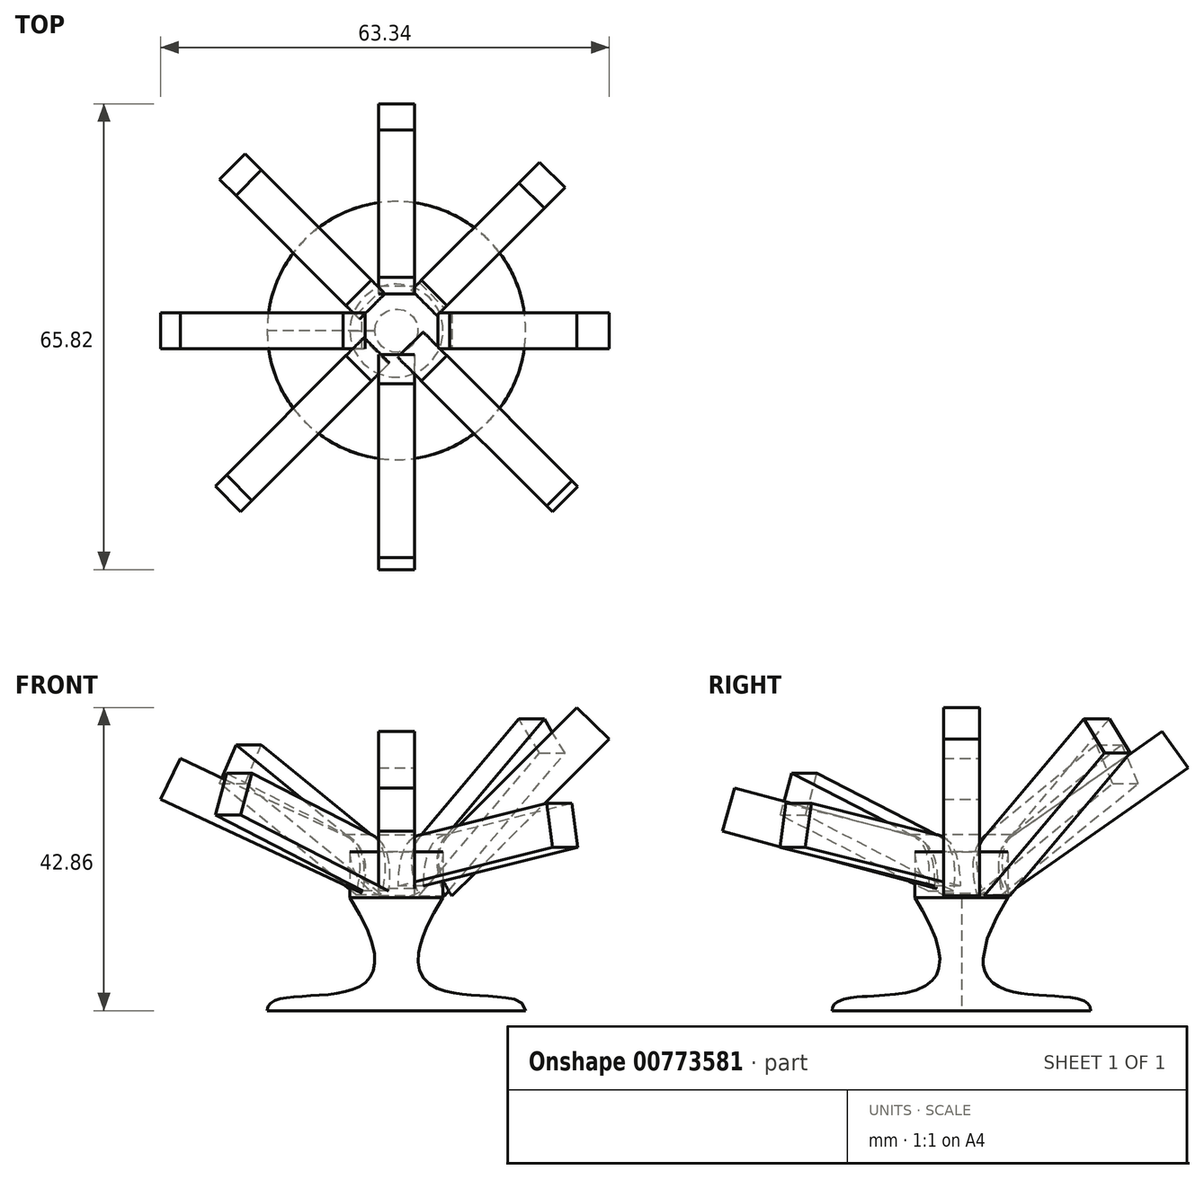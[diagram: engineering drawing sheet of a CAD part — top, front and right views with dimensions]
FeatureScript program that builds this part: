
annotation { "Feature Type Name" : "Feature", "Feature Type Description" : "" }
export const myFeature = defineFeature(function(context is Context, id is Id, definition is map)
    precondition{}
    {
        {
            assignVariable(context, id + "F0", {"name" : "First", "anyValue" : 45});
        }
        {
            assignVariable(context, id + "F1", {"name" : "delta", "anyValue" : -5});
        }
        {
            assignVariable(context, id + "F2", {"name" : "Count", "anyValue" : 8});
        }
        {
            var Q0;
            Q0=qCreatedBy(makeId("Front.planeOp"),FACE);
            var sketch = newSketch(context, id + "F3", { "sketchPlane" : qUnion([Q0])});
            skLineSegment(sketch, "E0", {"start": v(6.57, 22.45) * mm, "end": v(6.57, 15.95) * mm});
            skLineSegment(sketch, "E1", {"start": v(0, 0) * mm, "end": v(18.25, 0) * mm});
            skLineSegment(sketch, "E2", {"start": v(0, 0) * mm, "end": v(0, 28.99) * mm});
            skFitSpline(sketch, "E3", {"points": [v(6.57, 15.95) * mm, v(18.25, 0) * mm], "startDerivative": vector(-37.1, -59.05) * mm, "endDerivative": vector(-0.41, -15.66) * mm});
            skArc(sketch, "E4", {"start": v(6.57, 22.45) * mm, "mid": v(4.64, 27.09) * mm, "end": v(0, 28.99) * mm});
            skSolve(sketch);
        }
        {
            var Q0;
            Q0=makeQuery(id+"F3.imprint","IMPRINT",FACE,{"disambiguationData":[TD([[makeQuery(id+"F3.imprint","IMPRINT",EDGE,{"derivedFrom":sQuery(id+"F3.wireOp",EDGE,"E0")}),-1.0]])]});
            var Q1;
            Q1=sQuery(id+"F3.wireOp",EDGE,"E2");
            revolve(context, id + "F4", {"surfaceOperationType" : NewSurfaceOperationType.NEW, "entities" : qUnion([Q0]), "axis" : qUnion([Q1]), "revolveType" : RevolveType.FULL});
        }
        {
            var Q0;
            Q0=qCreatedBy(makeId("Front.planeOp"),FACE);
            var sketch = newSketch(context, id + "F5", { "sketchPlane" : qUnion([Q0])});
            skLineSegment(sketch, "E5", {"start": v(32.93, 24.9) * mm, "end": v(7.53, 24.9) * mm});
            skLineSegment(sketch, "E6", {"start": v(1.61, 18.55) * mm, "end": v(33, 18.55) * mm});
            skLineSegment(sketch, "E7", {"start": v(33, 18.55) * mm, "end": v(32.93, 24.9) * mm});
            skFitSpline(sketch, "E8", {"points": [v(7.53, 24.9) * mm, v(1.61, 18.55) * mm], "startDerivative": vector(-9.34, 0.31) * mm, "endDerivative": vector(-2.73, -13.53) * mm});
            skSolve(sketch);
        }
        {
            var Q0;
            Q0=makeQuery(id+"F5.imprint","IMPRINT",FACE,{"disambiguationData":[TD([[makeQuery(id+"F5.imprint","IMPRINT",EDGE,{"derivedFrom":sQuery(id+"F5.wireOp",EDGE,"E5")}),1.0]])]});
            extrude(context, id + "F6", {"entities" : qUnion([Q0]), "endBound" : BoundingType.SYMMETRIC, "oppositeDirection" : true, "depth" : 5.08 * mm, "offsetDistance" : 25.4 * mm});
        }
        {
            var Q0;
            Q0=makeQuery(id+"F6.opExtrude","SWEPT_BODY",BODY,{"disambiguationData":[OSD([sQuery(id+"F5.wireOp",EDGE,"E5"),sQuery(id+"F5.wireOp",EDGE,"E6"),sQuery(id+"F5.wireOp",EDGE,"E7"),sQuery(id+"F5.wireOp",EDGE,"E8")])]});
            var Q1;
            Q1=sQuery(id+"F3.wireOp",EDGE,"E2");
            circularPattern(context, id + "F7", {"entities" : qUnion([Q0]), "axis" : qUnion([Q1]), "angle" : 360 * degree, "instanceCount" : getVariable(context, 'Count'), "equalSpace" : true});
        }
        {
            var Q0;
            Q0=makeQuery(id+"F6.opExtrude","SWEPT_BODY",BODY,{"disambiguationData":[OSD([sQuery(id+"F5.wireOp",EDGE,"E5"),sQuery(id+"F5.wireOp",EDGE,"E6"),sQuery(id+"F5.wireOp",EDGE,"E7"),sQuery(id+"F5.wireOp",EDGE,"E8")])]});
            var Q1;
            Q1=makeQuery(id+"F6.opExtrude","SWEPT_EDGE",EDGE,{"disambiguationData":[OSD([sQuery(id+"F5.wireOp",EDGE,"E5"),sQuery(id+"F5.wireOp",EDGE,"E8")])]});
            transform(context, id + "F8", {"entities" : qUnion([Q0]), "transformType" : TransformType.ROTATION, "transformAxis" : qUnion([Q1]), "angle" : (getVariable(context, 'First')) * degree, "makeCopy" : false});
        }
        {
            var Q0;
            Q0=makeQuery(id+"F7.opPattern","COPY",BODY,{"derivedFrom":makeQuery(id+"F6.opExtrude","SWEPT_BODY",BODY,{"disambiguationData":[OSD([sQuery(id+"F5.wireOp",EDGE,"E5"),sQuery(id+"F5.wireOp",EDGE,"E6"),sQuery(id+"F5.wireOp",EDGE,"E7"),sQuery(id+"F5.wireOp",EDGE,"E8")])]}),"instanceName":"1"});
            var Q1;
            Q1=makeQuery(id+"F7.opPattern","COPY",EDGE,{"derivedFrom":makeQuery(id+"F6.opExtrude","SWEPT_EDGE",EDGE,{"disambiguationData":[OSD([sQuery(id+"F5.wireOp",EDGE,"E5"),sQuery(id+"F5.wireOp",EDGE,"E8")])]}),"instanceName":"1"});
            transform(context, id + "F9", {"entities" : qUnion([Q0]), "transformType" : TransformType.ROTATION, "transformAxis" : qUnion([Q1]), "angle" : (getVariable(context, 'First') + getVariable(context, 'delta')) * degree, "makeCopy" : false});
        }
        {
            var Q0;
            Q0=makeQuery(id+"F7.opPattern","COPY",BODY,{"derivedFrom":makeQuery(id+"F6.opExtrude","SWEPT_BODY",BODY,{"disambiguationData":[OSD([sQuery(id+"F5.wireOp",EDGE,"E5"),sQuery(id+"F5.wireOp",EDGE,"E6"),sQuery(id+"F5.wireOp",EDGE,"E7"),sQuery(id+"F5.wireOp",EDGE,"E8")])]}),"instanceName":"2"});
            var Q1;
            Q1=makeQuery(id+"F7.opPattern","COPY",EDGE,{"derivedFrom":makeQuery(id+"F6.opExtrude","SWEPT_EDGE",EDGE,{"disambiguationData":[OSD([sQuery(id+"F5.wireOp",EDGE,"E5"),sQuery(id+"F5.wireOp",EDGE,"E8")])]}),"instanceName":"2"});
            transform(context, id + "F10", {"entities" : qUnion([Q0]), "transformType" : TransformType.ROTATION, "transformAxis" : qUnion([Q1]), "angle" : (getVariable(context, 'First') + 2 * getVariable(context, 'delta')) * degree, "makeCopy" : false});
        }
        {
            var Q0;
            Q0=makeQuery(id+"F7.opPattern","COPY",BODY,{"derivedFrom":makeQuery(id+"F6.opExtrude","SWEPT_BODY",BODY,{"disambiguationData":[OSD([sQuery(id+"F5.wireOp",EDGE,"E5"),sQuery(id+"F5.wireOp",EDGE,"E6"),sQuery(id+"F5.wireOp",EDGE,"E7"),sQuery(id+"F5.wireOp",EDGE,"E8")])]}),"instanceName":"3"});
            var Q1;
            Q1=makeQuery(id+"F7.opPattern","COPY",EDGE,{"derivedFrom":makeQuery(id+"F6.opExtrude","SWEPT_EDGE",EDGE,{"disambiguationData":[OSD([sQuery(id+"F5.wireOp",EDGE,"E5"),sQuery(id+"F5.wireOp",EDGE,"E8")])]}),"instanceName":"3"});
            transform(context, id + "F11", {"entities" : qUnion([Q0]), "transformType" : TransformType.ROTATION, "transformAxis" : qUnion([Q1]), "angle" : (getVariable(context, 'First') + 3 * getVariable(context, 'delta')) * degree, "makeCopy" : false});
        }
        {
            var Q0;
            Q0=makeQuery(id+"F7.opPattern","COPY",BODY,{"derivedFrom":makeQuery(id+"F6.opExtrude","SWEPT_BODY",BODY,{"disambiguationData":[OSD([sQuery(id+"F5.wireOp",EDGE,"E5"),sQuery(id+"F5.wireOp",EDGE,"E6"),sQuery(id+"F5.wireOp",EDGE,"E7"),sQuery(id+"F5.wireOp",EDGE,"E8")])]}),"instanceName":"4"});
            var Q1;
            Q1=makeQuery(id+"F7.opPattern","COPY",EDGE,{"derivedFrom":makeQuery(id+"F6.opExtrude","SWEPT_EDGE",EDGE,{"disambiguationData":[OSD([sQuery(id+"F5.wireOp",EDGE,"E5"),sQuery(id+"F5.wireOp",EDGE,"E8")])]}),"instanceName":"4"});
            transform(context, id + "F12", {"entities" : qUnion([Q0]), "transformType" : TransformType.ROTATION, "transformAxis" : qUnion([Q1]), "angle" : (getVariable(context, 'First') + 4 * getVariable(context, 'delta')) * degree, "makeCopy" : false});
        }
        {
            var Q0;
            Q0=makeQuery(id+"F7.opPattern","COPY",BODY,{"derivedFrom":makeQuery(id+"F6.opExtrude","SWEPT_BODY",BODY,{"disambiguationData":[OSD([sQuery(id+"F5.wireOp",EDGE,"E5"),sQuery(id+"F5.wireOp",EDGE,"E6"),sQuery(id+"F5.wireOp",EDGE,"E7"),sQuery(id+"F5.wireOp",EDGE,"E8")])]}),"instanceName":"5"});
            var Q1;
            Q1=makeQuery(id+"F7.opPattern","COPY",EDGE,{"derivedFrom":makeQuery(id+"F6.opExtrude","SWEPT_EDGE",EDGE,{"disambiguationData":[OSD([sQuery(id+"F5.wireOp",EDGE,"E5"),sQuery(id+"F5.wireOp",EDGE,"E8")])]}),"instanceName":"5"});
            transform(context, id + "F13", {"entities" : qUnion([Q0]), "transformType" : TransformType.ROTATION, "transformAxis" : qUnion([Q1]), "angle" : (getVariable(context, 'First') + 5 * getVariable(context, 'delta')) * degree, "makeCopy" : false});
        }
        {
            var Q0;
            Q0=makeQuery(id+"F7.opPattern","COPY",BODY,{"derivedFrom":makeQuery(id+"F6.opExtrude","SWEPT_BODY",BODY,{"disambiguationData":[OSD([sQuery(id+"F5.wireOp",EDGE,"E5"),sQuery(id+"F5.wireOp",EDGE,"E6"),sQuery(id+"F5.wireOp",EDGE,"E7"),sQuery(id+"F5.wireOp",EDGE,"E8")])]}),"instanceName":"6"});
            var Q1;
            Q1=makeQuery(id+"F7.opPattern","COPY",EDGE,{"derivedFrom":makeQuery(id+"F6.opExtrude","SWEPT_EDGE",EDGE,{"disambiguationData":[OSD([sQuery(id+"F5.wireOp",EDGE,"E5"),sQuery(id+"F5.wireOp",EDGE,"E8")])]}),"instanceName":"6"});
            transform(context, id + "F14", {"entities" : qUnion([Q0]), "transformType" : TransformType.ROTATION, "transformAxis" : qUnion([Q1]), "angle" : (getVariable(context, 'First') + 6 * getVariable(context, 'delta')) * degree, "makeCopy" : false});
        }
        {
            var Q0;
            Q0=makeQuery(id+"F7.opPattern","COPY",BODY,{"derivedFrom":makeQuery(id+"F6.opExtrude","SWEPT_BODY",BODY,{"disambiguationData":[OSD([sQuery(id+"F5.wireOp",EDGE,"E5"),sQuery(id+"F5.wireOp",EDGE,"E6"),sQuery(id+"F5.wireOp",EDGE,"E7"),sQuery(id+"F5.wireOp",EDGE,"E8")])]}),"instanceName":"7"});
            var Q1;
            Q1=makeQuery(id+"F7.opPattern","COPY",EDGE,{"derivedFrom":makeQuery(id+"F6.opExtrude","SWEPT_EDGE",EDGE,{"disambiguationData":[OSD([sQuery(id+"F5.wireOp",EDGE,"E5"),sQuery(id+"F5.wireOp",EDGE,"E8")])]}),"instanceName":"7"});
            transform(context, id + "F15", {"entities" : qUnion([Q0]), "transformType" : TransformType.ROTATION, "transformAxis" : qUnion([Q1]), "angle" : (getVariable(context, 'First') + 7 * getVariable(context, 'delta')) * degree, "makeCopy" : false});
        }
    });
